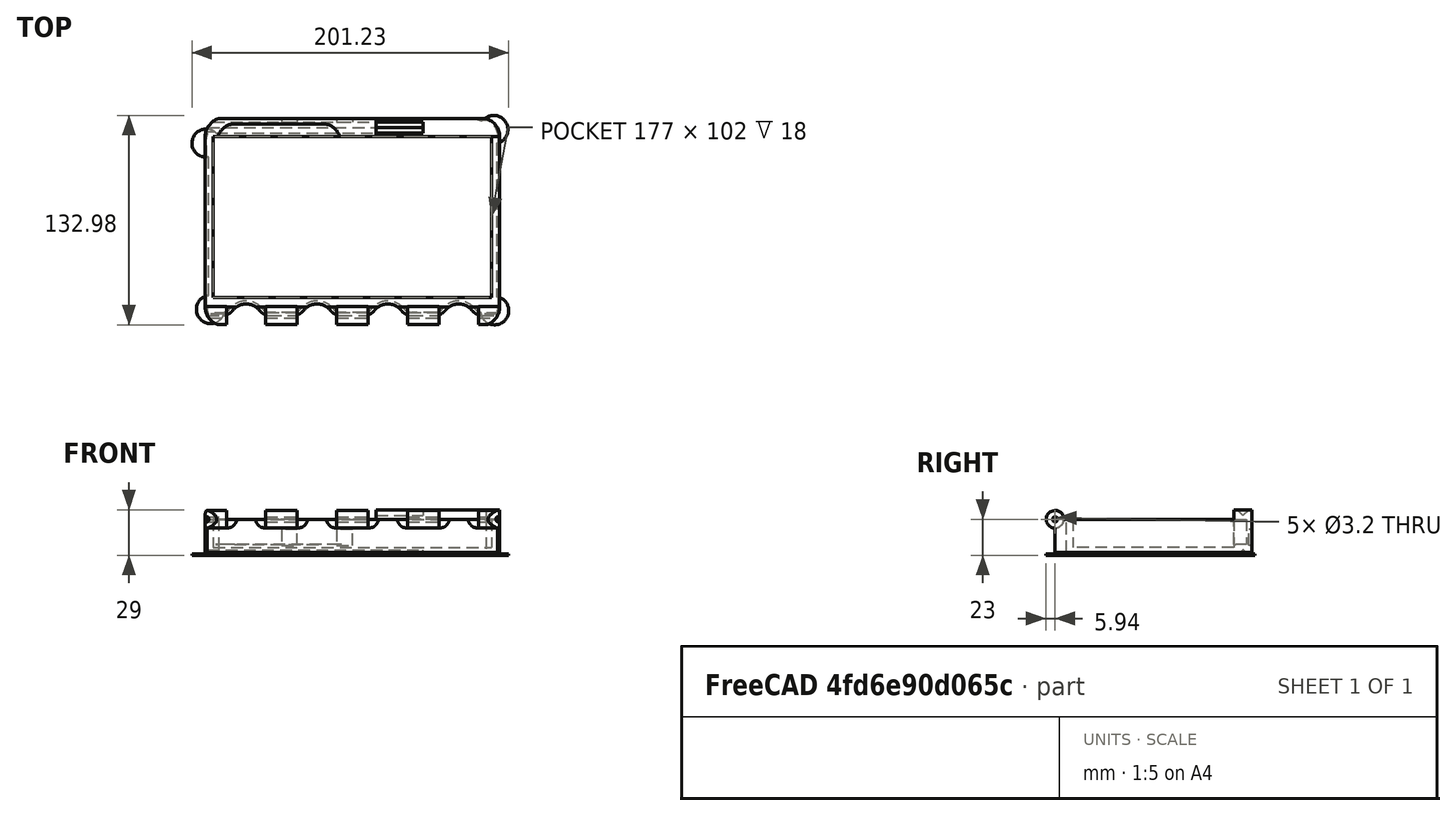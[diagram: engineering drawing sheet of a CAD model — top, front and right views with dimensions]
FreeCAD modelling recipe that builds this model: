
FCSTD DOCUMENT  (FreeCAD 0.19R)
Label: SwitchCaseSmallLatch3
License: All rights reserved
LicenseURL: http://en.wikipedia.org/wiki/All_rights_reserved
objects: Sketcher::SketchObject×13, PartDesign::Pocket×9, PartDesign::Pad×4, PartDesign::Chamfer×3, PartDesign::Fillet×2, PartDesign::LinearPattern×1, PartDesign::Body×1, Mesh::Feature×1
note: 51 computed .brp shape members not serialized (recipe doc carries the construction recipe); baked Part::Feature solids carry a one-line shape summary decoded from their .brp

FEATURE [Sketcher::SketchObject] Sketch
  FullyConstrained = true
  MapMode = 5
  Support = -> [XY_Plane]
  sketch-geometry (4):
    g0: LineSegment StartX=-100 StartY=62.5 StartZ=0 EndX=100 EndY=62.5 EndZ=0
    g1: LineSegment StartX=100 StartY=62.5 StartZ=0 EndX=100 EndY=-62.5 EndZ=0
    g2: LineSegment StartX=100 StartY=-62.5 StartZ=0 EndX=-100 EndY=-62.5 EndZ=0
    g3: LineSegment StartX=-100 StartY=-62.5 StartZ=0 EndX=-100 EndY=62.5 EndZ=0
  constraints (11):
    c: Coincident(g0,g1)
    c: Coincident(g1,g2)
    c: Coincident(g2,g3)
    c: Coincident(g3,g0)
    c: Horizontal(g0)
    c: Horizontal(g2)
    c: Vertical(g1)
    c: Vertical(g3)
    c: Symmetric(g0,g2,g-1)
    c: Distance(g0) = 200
    c: Distance(g1) = 125
FEATURE [PartDesign::Pad] Pad
  Direction = (1,1,1)
  Length = 23
  Length2 = 100
  Profile = -> Sketch
  Type = 0
FEATURE [Sketcher::SketchObject] Sketch001
  FullyConstrained = true
  MapMode = 5
  Placement = pos=(0,0,23) rot=(0,0,1;0rad)
  Support = -> [Pad]
  sketch-geometry (4):
    g0: LineSegment StartX=-88.5 StartY=51 StartZ=0 EndX=88.5 EndY=51 EndZ=0
    g1: LineSegment StartX=88.5 StartY=51 StartZ=0 EndX=88.5 EndY=-51 EndZ=0
    g2: LineSegment StartX=88.5 StartY=-51 StartZ=0 EndX=-88.5 EndY=-51 EndZ=0
    g3: LineSegment StartX=-88.5 StartY=-51 StartZ=0 EndX=-88.5 EndY=51 EndZ=0
  constraints (11):
    c: Coincident(g0,g1)
    c: Coincident(g1,g2)
    c: Coincident(g2,g3)
    c: Coincident(g3,g0)
    c: Horizontal(g0)
    c: Horizontal(g2)
    c: Vertical(g1)
    c: Vertical(g3)
    c: Symmetric(g0,g2,g-1)
    c: Distance(g0) = 177
    c: Distance(g1) = 102
FEATURE [PartDesign::Pocket] Pocket
  BaseFeature = -> Pad
  Length = 18
  Length2 = 100
  Profile = -> Sketch001
  Type = 0
FEATURE [Sketcher::SketchObject] Sketch002
  ExternalGeometry = -> [Pocket]
  FullyConstrained = true
  MapMode = 5
  Placement = pos=(100,0,0) rot=(0.57735,0.57735,0.57735;2.0944rad)
  Support = -> [Pocket]
  sketch-geometry (1):
    g0: Circle CenterX=-62.5 CenterY=23 CenterZ=0 NormalX=0 NormalY=0 NormalZ=1 AngleXU=0 Radius=5.5
  constraints (2):
    c: Radius(g0) = 5.5
    c: Coincident(g0,g-3)
FEATURE [PartDesign::Pocket] Pocket001
  BaseFeature = -> Pocket
  Length = 5
  Length2 = 100
  Profile = -> Sketch002
  Type = 1
FEATURE [Sketcher::SketchObject] Sketch004
  ExternalGeometry = -> [Pocket001]
  FullyConstrained = true
  MapMode = 5
  Placement = pos=(100,0,0) rot=(0.57735,0.57735,0.57735;2.0944rad)
  Support = -> [Pocket001]
  sketch-geometry (1):
    g0: Circle CenterX=-62.5 CenterY=23 CenterZ=0 NormalX=0 NormalY=0 NormalZ=1 AngleXU=0 Radius=5.6
  constraints (3):
    c: Radius(g0) = 5.6
    c: PointOnObject(g0,g-3)
    c: PointOnObject(g0,g-4)
FEATURE [PartDesign::Pad] Pad001  label="PadHinge"
  BaseFeature = -> Pocket001
  Direction = (1,1,1)
  Length = 20
  Length2 = 100
  Profile = -> Sketch004
  Reversed = true
  Type = 0
FEATURE [PartDesign::LinearPattern] LinearPattern
  BaseFeature = -> Pad001
  Direction = -> X_Axis
  Length = 180
  Occurrences = 5
  Originals = -> [Pad001]
  Reversed = true
FEATURE [Sketcher::SketchObject] Sketch005
  ExternalGeometry = -> [LinearPattern]
  FullyConstrained = true
  MapMode = 5
  Placement = pos=(100,0,0) rot=(0.57735,0.57735,0.57735;2.0944rad)
  Support = -> [LinearPattern]
  sketch-geometry (1):
    g0: Circle CenterX=-62.5 CenterY=23 CenterZ=0 NormalX=0 NormalY=0 NormalZ=1 AngleXU=0 Radius=1.6
  constraints (2):
    c: Radius(g0) = 1.6
    c: Coincident(g0,g-3)
FEATURE [PartDesign::Pocket] Pocket002
  BaseFeature = -> LinearPattern
  Length = 5
  Length2 = 100
  Profile = -> Sketch005
  Type = 1
FEATURE [Sketcher::SketchObject] Sketch007
  FullyConstrained = false
  MapMode = 5
  Placement = pos=(0,0,23) rot=(0,0,1;0rad)
  sketch-geometry (4):
    g0: LineSegment StartX=15 StartY=62.5 StartZ=0 EndX=100 EndY=62.5 EndZ=0
    g1: LineSegment StartX=100 StartY=62.5 StartZ=0 EndX=100 EndY=51 EndZ=0
    g2: LineSegment StartX=100 StartY=51 StartZ=0 EndX=15 EndY=51 EndZ=0
    g3: LineSegment StartX=15 StartY=51 StartZ=0 EndX=15 EndY=62.5 EndZ=0
  constraints (10):
    c: Coincident(g0,g1)
    c: Coincident(g1,g2)
    c: Coincident(g2,g3)
    c: Coincident(g3,g0)
    c: Horizontal(g0)
    c: Horizontal(g2)
    c: Vertical(g1)
    c: Vertical(g3)
    c: DistanceX(g0) = 15
    c: DistanceY(g0) = 62.5
FEATURE [PartDesign::Pad] Pad002  label="PadTower"
  BaseFeature = -> Pocket002
  Direction = (1,1,1)
  Length = 6
  Length2 = 100
  Profile = -> Sketch007
  Type = 0
FEATURE [Sketcher::SketchObject] Sketch008
  ExternalGeometry = -> [Pad002]
  FullyConstrained = true
  MapMode = 5
  Placement = pos=(-100,0,0) rot=(0.57735,-0.57735,-0.57735;2.0944rad)
  Support = -> [Pad002]
  sketch-geometry (8):
    g0: LineSegment StartX=-56.9645 StartY=3.53553 StartZ=0 EndX=-60.5 EndY=0 EndZ=0
    g1: LineSegment StartX=-60.5 StartY=0 StartZ=0 EndX=-56.9645 EndY=-3.53553 EndZ=0
    g2: LineSegment StartX=-56.9645 StartY=-3.53553 StartZ=0 EndX=-53.4289 EndY=0 EndZ=0
    g3: LineSegment StartX=-53.4289 StartY=0 StartZ=0 EndX=-56.9645 EndY=3.53553 EndZ=0
    g4: LineSegment StartX=-56.9645 StartY=32.5355 StartZ=0 EndX=-60.5 EndY=29 EndZ=0
    g5: LineSegment StartX=-60.5 StartY=29 StartZ=0 EndX=-56.9645 EndY=25.4645 EndZ=0
    g6: LineSegment StartX=-56.9645 StartY=25.4645 StartZ=0 EndX=-53.4289 EndY=29 EndZ=0
    g7: LineSegment StartX=-53.4289 StartY=29 StartZ=0 EndX=-56.9645 EndY=32.5355 EndZ=0
  constraints (24):
    c: Coincident(g0,g1)
    c: Coincident(g1,g2)
    c: Coincident(g2,g3)
    c: Coincident(g3,g0)
    c: Perpendicular(g0,g3)
    c: Perpendicular(g1,g0)
    c: Equal(g2,g1)
    c: Equal(g0,g3)
    c: Distance(g3) = 5
    c: PointOnObject(g2,g-1)
    c: PointOnObject(g0,g-1)
    c: Distance(g0,g-3) = 2
    c: Coincident(g4,g5)
    c: Coincident(g5,g6)
    c: Coincident(g6,g7)
    c: Coincident(g7,g4)
    c: Perpendicular(g4,g7)
    c: Perpendicular(g4,g5)
    c: Equal(g5,g6)
    c: Equal(g6,g7)
    c: Distance(g7) = 5
    c: PointOnObject(g4,g-4)
    c: PointOnObject(g6,g-4)
    c: Distance(g4,g-4) = 2
FEATURE [PartDesign::Pocket] Pocket003
  BaseFeature = -> Pad002
  Length = 145
  Length2 = 100
  Profile = -> Sketch008
  Type = 0
FEATURE [Sketcher::SketchObject] Sketch009
  FullyConstrained = true
  MapMode = 5
  Placement = pos=(0,0,0) rot=(1,0,0;3.14159rad)
  Support = -> [Pocket003]
  sketch-geometry (9):
    g0: ArcOfCircle CenterX=81.5 CenterY=57 CenterZ=0 NormalX=0 NormalY=0 NormalZ=1 AngleXU=0 Radius=12 StartAngle=0 EndAngle=1.5708
    g1: ArcOfCircle CenterX=81.5 CenterY=-51 CenterZ=0 NormalX=0 NormalY=0 NormalZ=1 AngleXU=0 Radius=12 StartAngle=4.71239 EndAngle=6.28319
    g2: ArcOfCircle CenterX=-81.5 CenterY=-51 CenterZ=0 NormalX=0 NormalY=0 NormalZ=1 AngleXU=0 Radius=12 StartAngle=3.14159 EndAngle=4.71239
    g3: ArcOfCircle CenterX=-81.5 CenterY=57 CenterZ=0 NormalX=0 NormalY=0 NormalZ=1 AngleXU=0 Radius=12 StartAngle=1.5708 EndAngle=3.14159
    g4: LineSegment StartX=-93.5 StartY=57 StartZ=0 EndX=-93.5 EndY=-51 EndZ=0
    g5: LineSegment StartX=-81.5 StartY=-63 StartZ=0 EndX=81.5 EndY=-63 EndZ=0
    g6: LineSegment StartX=93.5 StartY=-51 StartZ=0 EndX=93.5 EndY=57 EndZ=0
    g7: LineSegment StartX=81.5 StartY=69 StartZ=0 EndX=-81.5 EndY=69 EndZ=0
    g8: Circle CenterX=0 CenterY=0 CenterZ=0 NormalX=0 NormalY=0 NormalZ=1 AngleXU=0 Radius=141.94
  constraints (20):
    c: Radius(g3) = 12
    c: Equal(g3,g2)
    c: Equal(g3,g0)
    c: Tangent(g7,g3) = -1.5708
    c: Tangent(g7,g0) = -1.5708
    c: Tangent(g6,g0) = -1.5708
    c: Tangent(g6,g1) = -1.5708
    c: Tangent(g5,g2) = -1.5708
    c: Tangent(g4,g2) = -1.5708
    c: Tangent(g1,g5) = -1.5708
    c: Vertical(g4)
    c: Vertical(g6)
    c: Tangent(g4,g3) = -1.5708
    c: Symmetric(g1,g2,g-2)
    c: Symmetric(g0,g3,g-2)
    c: DistanceY(g0) = 69
    c: DistanceY(g1) = -63
    c: Distance(g2,g1) = 187
    c: Coincident(g8,g-1)
    c: Radius(g8) = 141.94
FEATURE [PartDesign::Pocket] Pocket004
  BaseFeature = -> Pocket003
  Length = 5
  Length2 = 100
  Profile = -> Sketch009
  Type = 1
FEATURE [Sketcher::SketchObject] Sketch010
  FullyConstrained = true
  MapMode = 5
  Placement = pos=(0,0,23) rot=(0,0,1;0rad)
  Support = -> [Pocket004]
  sketch-geometry (5):
    g0: Circle CenterX=-67.5 CenterY=-66.25 CenterZ=0 NormalX=0 NormalY=0 NormalZ=1 AngleXU=0 Radius=11
    g1: Circle CenterX=-22.5 CenterY=-66.25 CenterZ=0 NormalX=0 NormalY=0 NormalZ=1 AngleXU=0 Radius=11
    g2: Circle CenterX=22.5 CenterY=-66.25 CenterZ=0 NormalX=0 NormalY=0 NormalZ=1 AngleXU=0 Radius=11
    g3: Circle CenterX=67.5 CenterY=-66.25 CenterZ=0 NormalX=0 NormalY=0 NormalZ=1 AngleXU=0 Radius=11
    g4: LineSegment StartX=-100 StartY=-66.25 StartZ=0 EndX=100 EndY=-66.25 EndZ=0
  constraints (13):
    c: Radius(g3) = 11
    c: Equal(g3,g2)
    c: Equal(g3,g1)
    c: Equal(g3,g0)
    c: PointOnObject(g0,g4)
    c: PointOnObject(g1,g4)
    c: DistanceY(g4) = -66.25
    c: Symmetric(g2,g1,g-2)
    c: Symmetric(g3,g0,g-2)
    c: Distance(g2,g1) = 45
    c: Distance(g3,g0) = 135
    c: Distance(g4) = 200
    c: Symmetric(g4,g4,g-2)
FEATURE [PartDesign::Pocket] Pocket005
  BaseFeature = -> Pocket004
  Length = 5
  Length2 = 100
  Profile = -> Sketch010
  Type = 1
FEATURE [PartDesign::Fillet] Fillet
  Base = -> Pocket005 [Edge79,Edge81,Edge88,Edge90,Edge97,Edge99,Edge106,Edge108]
  BaseFeature = -> Pocket005
  Radius = 8
  SupportTransform = false
FEATURE [PartDesign::Chamfer] Chamfer
  Angle = 45
  Base = -> Fillet [Edge5]
  BaseFeature = -> Fillet
  ChamferType = 0
  FlipDirection = false
  Size = 2
  Size2 = 1
  SupportTransform = false
FEATURE [PartDesign::Chamfer] Chamfer001
  Angle = 45
  Base = -> Chamfer [Edge20]
  BaseFeature = -> Chamfer
  ChamferType = 0
  FlipDirection = false
  Size = 2
  Size2 = 1
  SupportTransform = false
FEATURE [PartDesign::Chamfer] Chamfer002
  Angle = 45
  Base = -> Chamfer001 [Edge14]
  BaseFeature = -> Chamfer001
  ChamferType = 0
  FlipDirection = false
  Size = 2
  Size2 = 1
  SupportTransform = false
FEATURE [Sketcher::SketchObject] Sketch011
  FullyConstrained = false
  MapMode = 5
  Placement = pos=(0,0,23) rot=(0,0,1;0rad)
  Support = -> [Chamfer002]
  sketch-geometry (4):
    g0: ArcOfCircle CenterX=-74.9627 CenterY=48.4724 CenterZ=0 NormalX=0 NormalY=0 NormalZ=1 AngleXU=0 Radius=10.6758 StartAngle=1.5708 EndAngle=4.71239
    g1: ArcOfCircle CenterX=-18.5759 CenterY=48.4724 CenterZ=0 NormalX=0 NormalY=0 NormalZ=1 AngleXU=0 Radius=10.6758 StartAngle=4.71239 EndAngle=7.85398
    g2: LineSegment StartX=-74.9627 StartY=37.7966 StartZ=0 EndX=-18.5759 EndY=37.7966 EndZ=0
    g3: LineSegment StartX=-74.9627 StartY=59.1482 StartZ=0 EndX=-18.5759 EndY=59.1482 EndZ=0
  constraints (6):
    c: Tangent(g0,g3) = 1.5708
    c: Tangent(g0,g2) = -1.5708
    c: Tangent(g2,g1) = -1.5708
    c: Tangent(g3,g1) = 1.5708
    c: Horizontal(g2)
    c: Equal(g0,g1)
FEATURE [PartDesign::Pocket] Pocket006
  BaseFeature = -> Chamfer002
  Length = 16
  Length2 = 100
  Profile = -> Sketch011
  Type = 0
FEATURE [Sketcher::SketchObject] Sketch012
  FullyConstrained = true
  MapMode = 5
  Placement = pos=(0,62.5,0) rot=(0,0.707107,0.707107;3.14159rad)
  Support = -> [Pocket006]
  sketch-geometry (8):
    g0: LineSegment StartX=35 StartY=16.5 StartZ=0 EndX=45 EndY=16.5 EndZ=0
    g1: LineSegment StartX=45 StartY=16.5 StartZ=0 EndX=45 EndY=6.5 EndZ=0
    g2: LineSegment StartX=45 StartY=6.5 StartZ=0 EndX=35 EndY=6.5 EndZ=0
    g3: LineSegment StartX=35 StartY=6.5 StartZ=0 EndX=35 EndY=16.5 EndZ=0
    g4: LineSegment StartX=0 StartY=16.5 StartZ=0 EndX=10 EndY=16.5 EndZ=0
    g5: LineSegment StartX=10 StartY=16.5 StartZ=0 EndX=10 EndY=6.5 EndZ=0
    g6: LineSegment StartX=10 StartY=6.5 StartZ=0 EndX=0 EndY=6.5 EndZ=0
    g7: LineSegment StartX=0 StartY=6.5 StartZ=0 EndX=0 EndY=16.5 EndZ=0
  constraints (24):
    c: Coincident(g0,g1)
    c: Coincident(g1,g2)
    c: Coincident(g2,g3)
    c: Coincident(g3,g0)
    c: Horizontal(g0)
    c: Horizontal(g2)
    c: Vertical(g1)
    c: Vertical(g3)
    c: Equal(g1,g0)
    c: Distance(g1) = 10
    c: DistanceY(g2) = 6.5
    c: DistanceX(g2) = 35
    c: Coincident(g4,g5)
    c: Coincident(g5,g6)
    c: Coincident(g6,g7)
    c: Coincident(g7,g4)
    c: Horizontal(g4)
    c: Horizontal(g6)
    c: Vertical(g5)
    c: Vertical(g7)
    c: Equal(g5,g6)
    c: Distance(g5) = 10
    c: DistanceY(g6) = 6.5
    c: PointOnObject(g4,g-2)
FEATURE [PartDesign::Pocket] Pocket007
  BaseFeature = -> Pocket006
  Length = 2
  Length2 = 100
  Profile = -> Sketch012
  Type = 0
FEATURE [PartDesign::Fillet] Fillet001
  Base = -> Pocket007 [Edge261,Edge259]
  BaseFeature = -> Pocket007
  Radius = 2
  SupportTransform = false
FEATURE [Sketcher::SketchObject] Sketch013
  FullyConstrained = true
  MapMode = 5
  Placement = pos=(0,0,29) rot=(0,0,1;0rad)
  Support = -> [Fillet001]
  sketch-geometry (4):
    g0: LineSegment StartX=0 StartY=51.25 StartZ=0 EndX=100 EndY=51.25 EndZ=0
    g1: LineSegment StartX=100 StartY=51.25 StartZ=0 EndX=100 EndY=46.18 EndZ=0
    g2: LineSegment StartX=100 StartY=46.18 StartZ=0 EndX=0 EndY=46.18 EndZ=0
    g3: LineSegment StartX=0 StartY=46.18 StartZ=0 EndX=0 EndY=51.25 EndZ=0
  constraints (12):
    c: Coincident(g0,g1)
    c: Coincident(g1,g2)
    c: Coincident(g2,g3)
    c: Coincident(g3,g0)
    c: Horizontal(g0)
    c: Horizontal(g2)
    c: Vertical(g1)
    c: Vertical(g3)
    c: DistanceY(g0) = 51.25
    c: PointOnObject(g0,g-2)
    c: Distance(g0) = 100
    c: Distance(g1) = 5.07
FEATURE [PartDesign::Pocket] Pocket008
  BaseFeature = -> Fillet001
  Length = 6
  Length2 = 100
  Profile = -> Sketch013
  Type = 0
FEATURE [Sketcher::SketchObject] Sketch014
  FullyConstrained = false
  MapMode = 5
  Placement = pos=(0,0,0) rot=(1,0,0;3.14159rad)
  Support = -> [Pocket008]
  sketch-geometry (4):
    g0: Circle CenterX=-90.1009 CenterY=58.646 CenterZ=0 NormalX=0 NormalY=0 NormalZ=1 AngleXU=0 Radius=9
    g1: Circle CenterX=90.31 CenterY=59.4368 CenterZ=0 NormalX=0 NormalY=0 NormalZ=1 AngleXU=0 Radius=9
    g2: Circle CenterX=89.7782 CenterY=-55.5417 CenterZ=0 NormalX=0 NormalY=0 NormalZ=1 AngleXU=0 Radius=9
    g3: Circle CenterX=-92.9175 CenterY=-46.9608 CenterZ=0 NormalX=0 NormalY=0 NormalZ=1 AngleXU=0 Radius=9
  constraints (4):
    c: Radius(g3) = 9
    c: Equal(g3,g2)
    c: Equal(g3,g1)
    c: Equal(g3,g0)
FEATURE [PartDesign::Pad] Pad003
  BaseFeature = -> Pocket008
  Direction = (1,1,1)
  Length = 1
  Length2 = 100
  Profile = -> Sketch014
  Reversed = true
  Type = 0
FEATURE [PartDesign::Body] Body
  Group = -> [Sketch,Pad,Sketch001,Pocket,Sketch002,Pocket001,Sketch004,Pad001,LinearPattern,Sketch005,Pocket002,Sketch007,Pad002,Sketch008,Pocket003,Sketch009,Pocket004,Sketch010,Pocket005,Fillet,Chamfer,Chamfer001,Chamfer002,Sketch011,Pocket006,Sketch012,Pocket007,Fillet001,Sketch013,Pocket008,Sketch014,Pad003]
  Origin = -> Origin
  Tip = -> Pad003
FEATURE [Mesh::Feature] Mesh  label="Pad003 (Meshed)"
